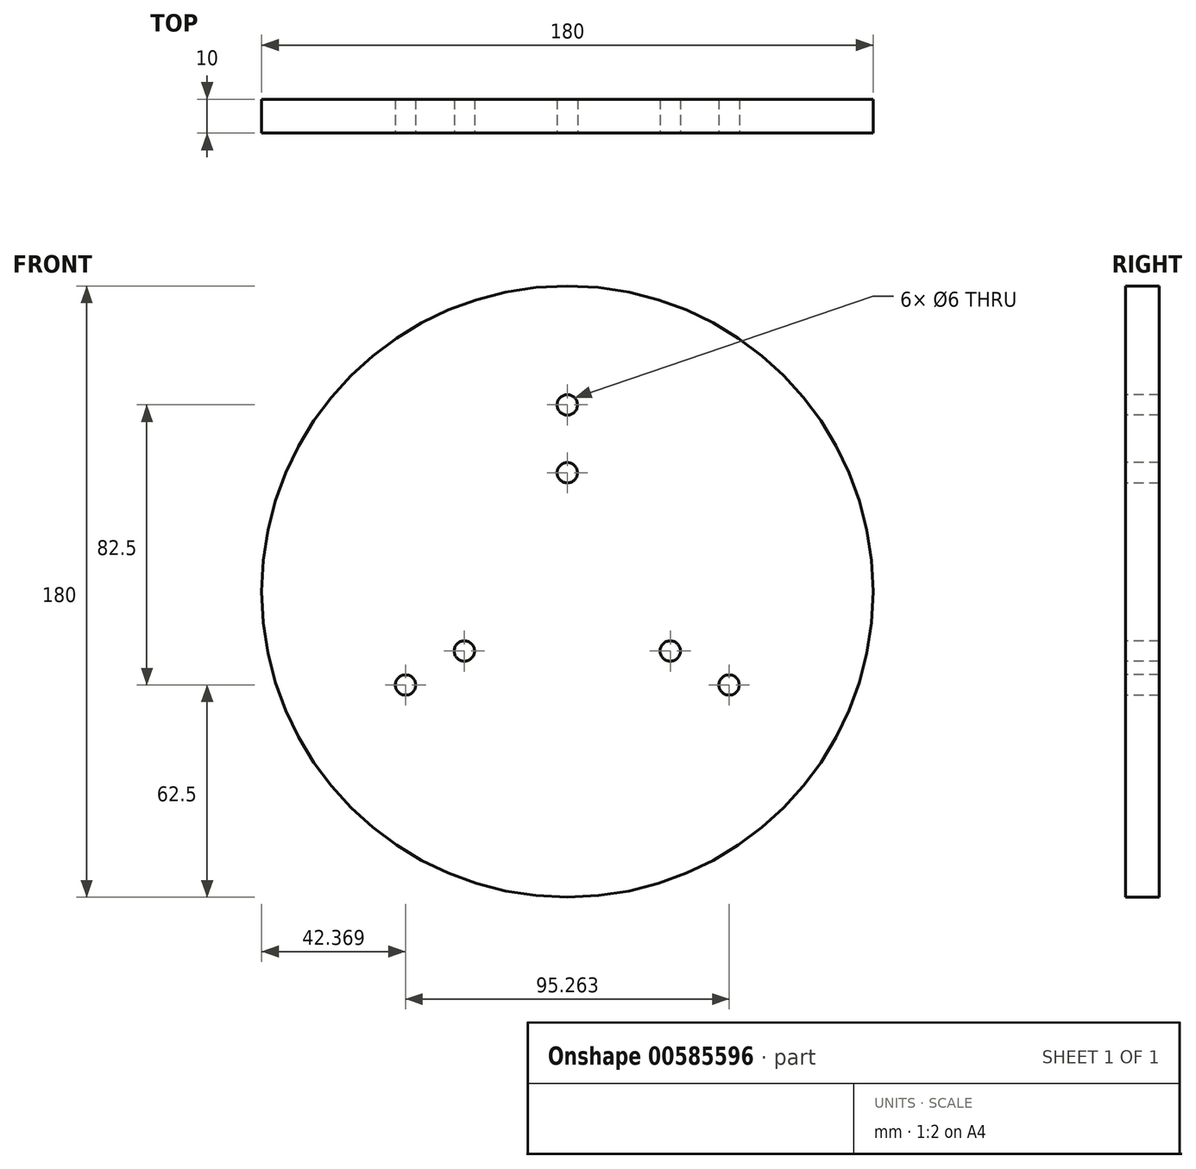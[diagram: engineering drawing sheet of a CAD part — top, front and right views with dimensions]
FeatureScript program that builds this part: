
annotation { "Feature Type Name" : "Feature", "Feature Type Description" : "" }
export const myFeature = defineFeature(function(context is Context, id is Id, definition is map)
    precondition{}
    {
        {
            var Q0;
            Q0=qCreatedBy(makeId("Front.planeOp"),FACE);
            var sketch = newSketch(context, id + "F0", { "sketchPlane" : qUnion([Q0])});
            skLineSegment(sketch, "E0.bottom", {"start": v(90, -90) * mm, "end": v(-90, -90) * mm});
            skLineSegment(sketch, "E0.top", {"start": v(90, 90) * mm, "end": v(-90, 90) * mm});
            skLineSegment(sketch, "E0.left", {"start": v(90, -90) * mm, "end": v(90, 90) * mm});
            skLineSegment(sketch, "E0.right", {"start": v(-90, -90) * mm, "end": v(-90, 90) * mm});
            skPoint(sketch, "E0.middle", {"position": v(0, 0) * mm});
            skSolve(sketch);
        }
        {
            var Q0;
            Q0 = qSketchRegion(id + "F0", true);
            extrude(context, id + "F1", {"entities" : qUnion([Q0]), "oppositeDirection" : true, "depth" : 10 * mm, "offsetDistance" : 25 * mm});
        }
        {
            var Q0;
            Q0=makeQuery(id+"F0.imprint","IMPRINT",FACE,{"disambiguationData":[TD([[makeQuery(id+"F0.imprint","IMPRINT",EDGE,{"derivedFrom":sQuery(id+"F0.wireOp",EDGE,"E0.bottom")}),-1.0]])]});
            var sketch = newSketch(context, id + "F2", { "sketchPlane" : qUnion([Q0])});
            skPoint(sketch, "E1.middle", {"position": v(0, 0) * mm});
            skLineSegment(sketch, "E2", {"start": v(0, 90) * mm, "end": v(0, 0) * mm, "construction": true});
            skCircle(sketch, "E3", {"center": v(0, 55) * mm, "radius": 3 * mm});
            skCircle(sketch, "E4", {"center": v(0, 35) * mm, "radius": 3 * mm});
            skLineSegment(sketch, "E5.1.0", {"start": v(-77.94, -45) * mm, "end": v(0, 0) * mm, "construction": true});
            skCircle(sketch, "E5.1.1", {"center": v(-30.31, -17.5) * mm, "radius": 3 * mm});
            skCircle(sketch, "E5.1.2", {"center": v(-47.63, -27.5) * mm, "radius": 3 * mm});
            skLineSegment(sketch, "E5.2.0", {"start": v(77.94, -45) * mm, "end": v(0, 0) * mm, "construction": true});
            skCircle(sketch, "E5.2.1", {"center": v(30.31, -17.5) * mm, "radius": 3 * mm});
            skCircle(sketch, "E5.2.2", {"center": v(47.63, -27.5) * mm, "radius": 3 * mm});
            skSolve(sketch);
        }
        {
            var Q0;
            Q0 = qSketchRegion(id + "F2", true);
            extrude(context, id + "F3", {"entities" : qUnion([Q0]), "operationType" : NewBodyOperationType.REMOVE, "endBound" : BoundingType.THROUGH_ALL, "oppositeDirection" : true, "depth" : 1 * mm, "offsetDistance" : 25 * mm});
        }
        {
            var Q0;
            Q0=makeQuery(id+"F0.imprint","IMPRINT",FACE,{"disambiguationData":[TD([[makeQuery(id+"F0.imprint","IMPRINT",EDGE,{"derivedFrom":sQuery(id+"F0.wireOp",EDGE,"E0.bottom")}),-1.0]])]});
            var sketch = newSketch(context, id + "F4", { "sketchPlane" : qUnion([Q0])});
            skCircle(sketch, "E6", {"center": v(0, 0) * mm, "radius": 90 * mm});
            skSolve(sketch);
        }
        {
            var Q0;
            {var subQ0=sQuery(id+"F4.wireOp",EDGE,"E6");var subQ1=makeQuery(id+"F0.imprint","IMPRINT",EDGE,{"derivedFrom":sQuery(id+"F0.wireOp",EDGE,"E0.top")});var subQ2=makeQuery(id+"F4.imprint","INTERSECT",VERTEX,{"derivedFrom":[subQ1,subQ0]});Q0=makeQuery(id+"F4.imprint","IMPRINT",FACE,{"disambiguationData":[TD([[makeQuery(id+"F4.imprint","IMPRINT",EDGE,{"disambiguationData":[TD([[subQ2,-1.0]])],"derivedFrom":subQ0}),-1.0]])]});}
            var Q1;
            {var subQ0=sQuery(id+"F4.wireOp",EDGE,"E6");var subQ1=makeQuery(id+"F0.imprint","IMPRINT",EDGE,{"derivedFrom":sQuery(id+"F0.wireOp",EDGE,"E0.top")});var subQ2=makeQuery(id+"F4.imprint","INTERSECT",VERTEX,{"derivedFrom":[subQ1,subQ0]});Q1=makeQuery(id+"F4.imprint","IMPRINT",FACE,{"disambiguationData":[TD([[makeQuery(id+"F4.imprint","IMPRINT",EDGE,{"disambiguationData":[TD([[subQ2,1.0]])],"derivedFrom":subQ0}),-1.0]])]});}
            var Q2;
            {var subQ0=sQuery(id+"F4.wireOp",EDGE,"E6");var subQ1=makeQuery(id+"F0.imprint","IMPRINT",EDGE,{"derivedFrom":sQuery(id+"F0.wireOp",EDGE,"E0.left")});var subQ2=makeQuery(id+"F4.imprint","INTERSECT",VERTEX,{"derivedFrom":[subQ1,subQ0]});Q2=makeQuery(id+"F4.imprint","IMPRINT",FACE,{"disambiguationData":[TD([[makeQuery(id+"F4.imprint","IMPRINT",EDGE,{"disambiguationData":[TD([[subQ2,1.0]])],"derivedFrom":subQ0}),-1.0]])]});}
            var Q3;
            {var subQ0=sQuery(id+"F4.wireOp",EDGE,"E6");var subQ1=makeQuery(id+"F0.imprint","IMPRINT",EDGE,{"derivedFrom":sQuery(id+"F0.wireOp",EDGE,"E0.right")});var subQ2=makeQuery(id+"F4.imprint","INTERSECT",VERTEX,{"derivedFrom":[subQ1,subQ0]});Q3=makeQuery(id+"F4.imprint","IMPRINT",FACE,{"disambiguationData":[TD([[makeQuery(id+"F4.imprint","IMPRINT",EDGE,{"disambiguationData":[TD([[subQ2,-1.0]])],"derivedFrom":subQ0}),-1.0]])]});}
            extrude(context, id + "F5", {"entities" : qUnion([Q0, Q1, Q2, Q3]), "operationType" : NewBodyOperationType.REMOVE, "endBound" : BoundingType.THROUGH_ALL, "oppositeDirection" : true, "depth" : 25 * mm, "offsetDistance" : 25 * mm});
        }
    });
